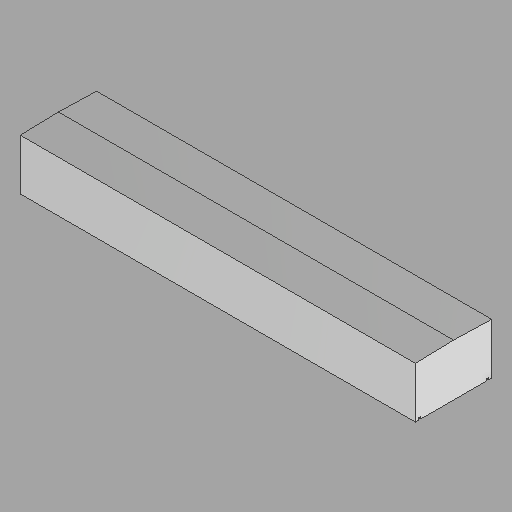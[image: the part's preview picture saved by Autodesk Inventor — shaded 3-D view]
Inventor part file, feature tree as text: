
AUTODESK INVENTOR PART (.ipt)
format: ipt  version: 2022.2 (Build 262287010, 287A)  size: 141,824 bytes
history: native  units: in
note: dims shown in document units (in); Inventor stores cm internally (conversion verified against a paired STEP export)
features: extrude x2, sketch x1, other x1
ambient origin geometry x8: Origin, YZ Plane, XZ Plane, XY Plane, X Axis, Y Axis, Z Axis, Center Point
bodies: Solid1 (feature_tree)
feature tree (4):
  sketch  "Sketch1"  dims[d0=0.125in d1=0.25in d2=0.25in d3=0.375in d4=0.25in d5=0.25in d6=0.375in d7=46.625in d8=0.0in d9=46.625in d10=0.0in]
  extrude  "Extrusion1"  Depth=0.25in
  extrude  "Extrusion2"  Depth=0.25in
  other  "Cap (3)"
